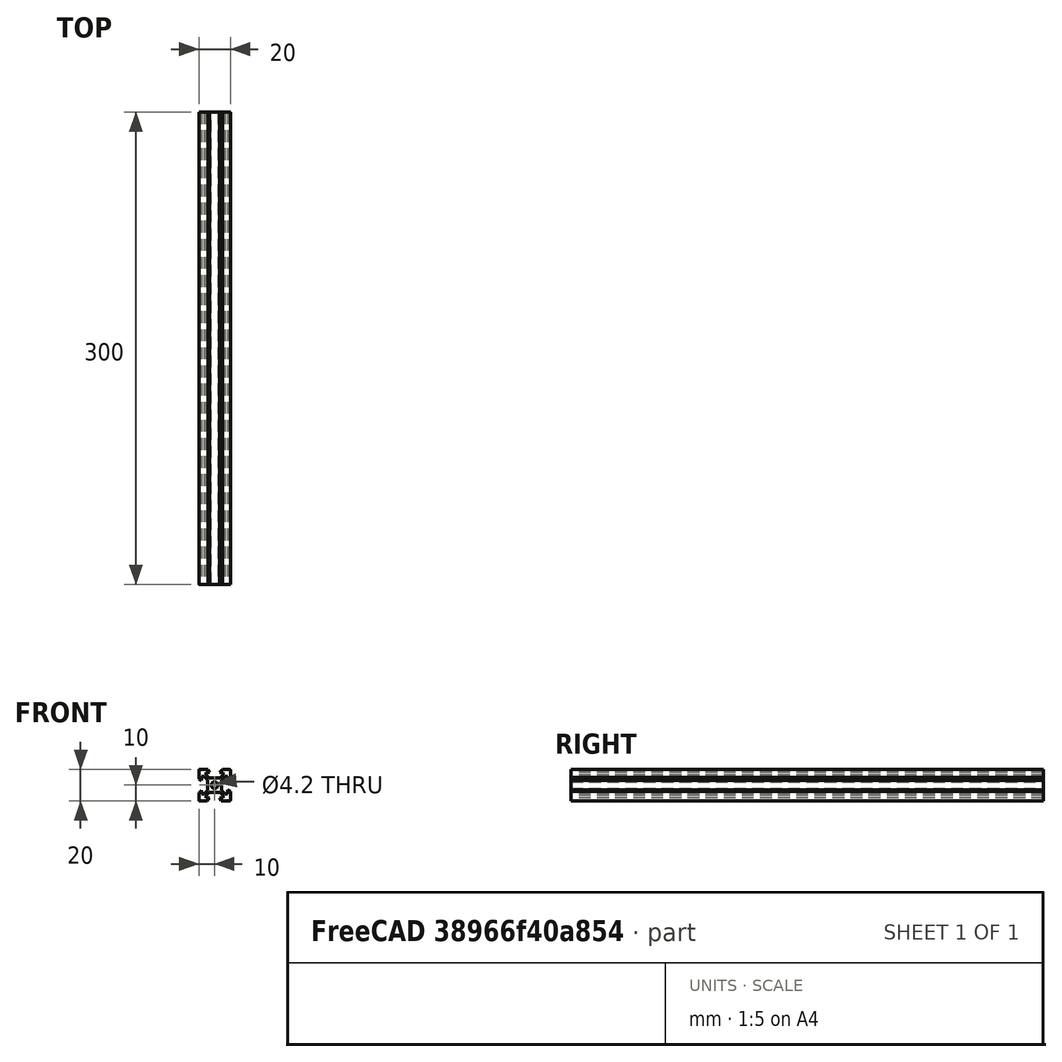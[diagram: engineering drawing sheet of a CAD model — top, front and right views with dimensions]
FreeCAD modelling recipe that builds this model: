
FCSTD DOCUMENT  (FreeCAD 0.20R29177 (Git))
Label: Slotted extrusion
License: All rights reserved
objects: Sketcher::SketchObject×1, PartDesign::Pad×1, PartDesign::Body×1
note: 4 computed .brp shape members not serialized (recipe doc carries the construction recipe); baked Part::Feature solids carry a one-line shape summary decoded from their .brp

FEATURE [Sketcher::SketchObject] Sketch
  FullyConstrained = true
  MapMode = 5
  Placement = pos=(0,0,0) rot=(1,0,0;1.5708rad)
  Support = -> [XZ_Plane]
  sketch-geometry (109):
    g0: LineSegment StartX=-10 StartY=10 StartZ=0 EndX=10 EndY=10 EndZ=0
    g1: LineSegment StartX=10 StartY=10 StartZ=0 EndX=10 EndY=-10 EndZ=0
    g2: LineSegment StartX=10 StartY=-10 StartZ=0 EndX=-10 EndY=-10 EndZ=0
    g3: LineSegment StartX=-10 StartY=-10 StartZ=0 EndX=-10 EndY=10 EndZ=0
    g4: LineSegment StartX=-8.2 StartY=8.2 StartZ=0 EndX=8.2 EndY=8.2 EndZ=0
    g5: LineSegment StartX=8.2 StartY=8.2 StartZ=0 EndX=8.2 EndY=-8.2 EndZ=0
    g6: LineSegment StartX=8.2 StartY=-8.2 StartZ=0 EndX=-8.2 EndY=-8.2 EndZ=0
    g7: LineSegment StartX=-8.2 StartY=-8.2 StartZ=0 EndX=-8.2 EndY=8.2 EndZ=0
    g8: LineSegment StartX=-4.5 StartY=4.5 StartZ=0 EndX=4.5 EndY=4.5 EndZ=0
    g9: LineSegment StartX=4.5 StartY=4.5 StartZ=0 EndX=4.5 EndY=-4.5 EndZ=0
    g10: LineSegment StartX=4.5 StartY=-4.5 StartZ=0 EndX=-4.5 EndY=-4.5 EndZ=0
    g11: LineSegment StartX=-4.5 StartY=-4.5 StartZ=0 EndX=-4.5 EndY=4.5 EndZ=0
    g12: LineSegment StartX=-8.2 StartY=5.5 StartZ=0 EndX=-8.2 EndY=3.1 EndZ=0
    g13: LineSegment StartX=-10 StartY=4.1 StartZ=0 EndX=-10 EndY=9.5 EndZ=0
    g14: LineSegment StartX=-9.5 StartY=10 StartZ=0 EndX=-4.1 EndY=10 EndZ=0
    g15: LineSegment StartX=-4.1 StartY=10 StartZ=0 EndX=-3.1 EndY=8.2 EndZ=0
    g16: LineSegment StartX=-3.1 StartY=8.2 StartZ=0 EndX=-5.5 EndY=8.2 EndZ=0
    g17: LineSegment StartX=3.1 StartY=8.2 StartZ=0 EndX=4.9 EndY=10 EndZ=0
    g18: LineSegment StartX=4.9 StartY=10 StartZ=0 EndX=9.5 EndY=10 EndZ=0
    g19: LineSegment StartX=10 StartY=9.5 StartZ=0 EndX=10 EndY=4.9 EndZ=0
    g20: LineSegment StartX=10 StartY=4.9 StartZ=0 EndX=8.2 EndY=3.1 EndZ=0
    g21: LineSegment StartX=-8.2 StartY=8.2 StartZ=0 EndX=-5.5 EndY=8.2 EndZ=0
    g22: LineSegment StartX=-5.5 StartY=8.2 StartZ=0 EndX=-5.5 EndY=5.5 EndZ=0
    g23: LineSegment StartX=-5.5 StartY=5.5 StartZ=0 EndX=-8.2 EndY=5.5 EndZ=0
    g24: LineSegment StartX=-8.2 StartY=5.5 StartZ=0 EndX=-8.2 EndY=8.2 EndZ=0
    g25: LineSegment StartX=5.5 StartY=8.2 StartZ=0 EndX=8.2 EndY=8.2 EndZ=0
    g26: LineSegment StartX=8.2 StartY=8.2 StartZ=0 EndX=8.2 EndY=5.5 EndZ=0
    g27: LineSegment StartX=8.2 StartY=5.5 StartZ=0 EndX=5.5 EndY=5.5 EndZ=0
    g28: LineSegment StartX=5.5 StartY=5.5 StartZ=0 EndX=5.5 EndY=8.2 EndZ=0
    g29: LineSegment StartX=3.1 StartY=8.2 StartZ=0 EndX=5.5 EndY=8.2 EndZ=0
    g30: LineSegment StartX=8.2 StartY=3.1 StartZ=0 EndX=8.2 EndY=5.5 EndZ=0
    g31: LineSegment StartX=-4.5 StartY=4.5 StartZ=0 EndX=-3.43934 EndY=4.5 EndZ=0
    g32: LineSegment StartX=-3.43934 StartY=4.5 StartZ=0 EndX=-3.43934 EndY=3.43934 EndZ=0
    g33: LineSegment StartX=-3.43934 StartY=3.43934 StartZ=0 EndX=-4.5 EndY=3.43934 EndZ=0
    g34: LineSegment StartX=-4.5 StartY=3.43934 StartZ=0 EndX=-4.5 EndY=4.5 EndZ=0
    g35: LineSegment StartX=-6.56066 StartY=6.56066 StartZ=0 EndX=-5.5 EndY=6.56066 EndZ=0
    g36: LineSegment StartX=-5.5 StartY=6.56066 StartZ=0 EndX=-5.5 EndY=5.5 EndZ=0
    g37: LineSegment StartX=-5.5 StartY=5.5 StartZ=0 EndX=-6.56066 EndY=5.5 EndZ=0
    g38: LineSegment StartX=-6.56066 StartY=5.5 StartZ=0 EndX=-6.56066 EndY=6.56066 EndZ=0
    g39: LineSegment StartX=-8.2 StartY=5.5 StartZ=0 EndX=-6.56066 EndY=5.5 EndZ=0
    g40: LineSegment StartX=-6.56066 StartY=5.5 StartZ=0 EndX=-4.5 EndY=3.43934 EndZ=0
    g41: LineSegment StartX=-5.5 StartY=8.2 StartZ=0 EndX=-5.5 EndY=6.56066 EndZ=0
    g42: LineSegment StartX=-3.43934 StartY=4.5 StartZ=0 EndX=-5.5 EndY=6.56066 EndZ=0
    g43: LineSegment StartX=3.43934 StartY=4.5 StartZ=0 EndX=4.5 EndY=4.5 EndZ=0
    g44: LineSegment StartX=4.5 StartY=4.5 StartZ=0 EndX=4.5 EndY=3.43934 EndZ=0
    g45: LineSegment StartX=4.5 StartY=3.43934 StartZ=0 EndX=3.43934 EndY=3.43934 EndZ=0
    g46: LineSegment StartX=3.43934 StartY=3.43934 StartZ=0 EndX=3.43934 EndY=4.5 EndZ=0
    g47: LineSegment StartX=5.5 StartY=6.56066 StartZ=0 EndX=6.56066 EndY=6.56066 EndZ=0
    g48: LineSegment StartX=6.56066 StartY=6.56066 StartZ=0 EndX=6.56066 EndY=5.5 EndZ=0
    g49: LineSegment StartX=6.56066 StartY=5.5 StartZ=0 EndX=5.5 EndY=5.5 EndZ=0
    g50: LineSegment StartX=5.5 StartY=5.5 StartZ=0 EndX=5.5 EndY=6.56066 EndZ=0
    g51: LineSegment StartX=8.2 StartY=5.5 StartZ=0 EndX=6.56066 EndY=5.5 EndZ=0
    g52: LineSegment StartX=6.56066 StartY=5.5 StartZ=0 EndX=4.5 EndY=3.43934 EndZ=0
    g53: LineSegment StartX=5.5 StartY=8.2 StartZ=0 EndX=5.5 EndY=6.56066 EndZ=0
    g54: LineSegment StartX=5.5 StartY=6.56066 StartZ=0 EndX=3.43934 EndY=4.5 EndZ=0
    g55: LineSegment StartX=3.43934 StartY=4.5 StartZ=0 EndX=-3.43934 EndY=4.5 EndZ=0
    g56: LineSegment StartX=4.5 StartY=3.43934 StartZ=0 EndX=4.5 EndY=-3.43934 EndZ=0
    g57: LineSegment StartX=8.2 StartY=-8.2 StartZ=0 EndX=5.5 EndY=-8.2 EndZ=0
    g58: LineSegment StartX=5.5 StartY=-8.2 StartZ=0 EndX=5.5 EndY=-5.5 EndZ=0
    g59: LineSegment StartX=5.5 StartY=-5.5 StartZ=0 EndX=8.2 EndY=-5.5 EndZ=0
    g60: LineSegment StartX=8.2 StartY=-5.5 StartZ=0 EndX=8.2 EndY=-8.2 EndZ=0
    g61: LineSegment StartX=3.43934 StartY=-3.43934 StartZ=0 EndX=4.5 EndY=-3.43934 EndZ=0
    g62: LineSegment StartX=4.5 StartY=-3.43934 StartZ=0 EndX=4.5 EndY=-4.5 EndZ=0
    g63: LineSegment StartX=4.5 StartY=-4.5 StartZ=0 EndX=3.43934 EndY=-4.5 EndZ=0
    g64: LineSegment StartX=3.43934 StartY=-4.5 StartZ=0 EndX=3.43934 EndY=-3.43934 EndZ=0
    g65: LineSegment StartX=5.5 StartY=-5.5 StartZ=0 EndX=6.56066 EndY=-5.5 EndZ=0
    g66: LineSegment StartX=6.56066 StartY=-5.5 StartZ=0 EndX=6.56066 EndY=-6.56066 EndZ=0
    g67: LineSegment StartX=6.56066 StartY=-6.56066 StartZ=0 EndX=5.5 EndY=-6.56066 EndZ=0
    g68: LineSegment StartX=5.5 StartY=-6.56066 StartZ=0 EndX=5.5 EndY=-5.5 EndZ=0
    g69: LineSegment StartX=4.5 StartY=-3.43934 StartZ=0 EndX=6.56066 EndY=-5.5 EndZ=0
    g70: LineSegment StartX=5.5 StartY=-6.56066 StartZ=0 EndX=3.43934 EndY=-4.5 EndZ=0
    g71: LineSegment StartX=6.56066 StartY=-5.5 StartZ=0 EndX=8.2 EndY=-5.5 EndZ=0
    g72: LineSegment StartX=8.2 StartY=-5.5 StartZ=0 EndX=8.2 EndY=-3.1 EndZ=0
    g73: LineSegment StartX=8.2 StartY=-3.1 StartZ=0 EndX=10 EndY=-4.1 EndZ=0
    g74: LineSegment StartX=10 StartY=-4.1 StartZ=0 EndX=10 EndY=-9.5 EndZ=0
    g75: LineSegment StartX=3.1 StartY=-8.2 StartZ=0 EndX=5.5 EndY=-8.2 EndZ=0
    g76: LineSegment StartX=5.5 StartY=-8.2 StartZ=0 EndX=5.5 EndY=-6.56066 EndZ=0
    g77: LineSegment StartX=4.1 StartY=-10 StartZ=0 EndX=9.5 EndY=-10 EndZ=0
    g78: LineSegment StartX=4.1 StartY=-10 StartZ=0 EndX=3.1 EndY=-8.2 EndZ=0
    g79: LineSegment StartX=-10 StartY=4.1 StartZ=0 EndX=-8.2 EndY=3.1 EndZ=0
    g80: LineSegment StartX=-4.5 StartY=-3.43934 StartZ=0 EndX=-3.43934 EndY=-3.43934 EndZ=0
    g81: LineSegment StartX=-3.43934 StartY=-3.43934 StartZ=0 EndX=-3.43934 EndY=-4.5 EndZ=0
    g82: LineSegment StartX=-3.43934 StartY=-4.5 StartZ=0 EndX=-4.5 EndY=-4.5 EndZ=0
    g83: LineSegment StartX=-4.5 StartY=-4.5 StartZ=0 EndX=-4.5 EndY=-3.43934 EndZ=0
    g84: LineSegment StartX=-8.2 StartY=-5.5 StartZ=0 EndX=-5.5 EndY=-5.5 EndZ=0
    g85: LineSegment StartX=-5.5 StartY=-5.5 StartZ=0 EndX=-5.5 EndY=-8.2 EndZ=0
    g86: LineSegment StartX=-5.5 StartY=-8.2 StartZ=0 EndX=-8.2 EndY=-8.2 EndZ=0
    g87: LineSegment StartX=-8.2 StartY=-8.2 StartZ=0 EndX=-8.2 EndY=-5.5 EndZ=0
    g88: LineSegment StartX=-6.56066 StartY=-5.5 StartZ=0 EndX=-5.5 EndY=-5.5 EndZ=0
    g89: LineSegment StartX=-5.5 StartY=-5.5 StartZ=0 EndX=-5.5 EndY=-6.56066 EndZ=0
    g90: LineSegment StartX=-5.5 StartY=-6.56066 StartZ=0 EndX=-6.56066 EndY=-6.56066 EndZ=0
    g91: LineSegment StartX=-6.56066 StartY=-6.56066 StartZ=0 EndX=-6.56066 EndY=-5.5 EndZ=0
    g92: LineSegment StartX=-5.5 StartY=-6.56066 StartZ=0 EndX=-3.43934 EndY=-4.5 EndZ=0
    g93: LineSegment StartX=-3.43934 StartY=-4.5 StartZ=0 EndX=3.43934 EndY=-4.5 EndZ=0
    g94: LineSegment StartX=-5.5 StartY=-6.56066 StartZ=0 EndX=-5.5 EndY=-8.2 EndZ=0
    g95: LineSegment StartX=-5.5 StartY=-8.2 StartZ=0 EndX=-3.2 EndY=-8.2 EndZ=0
    g96: LineSegment StartX=-3.2 StartY=-8.2 StartZ=0 EndX=-4.9 EndY=-10 EndZ=0
    g97: LineSegment StartX=-4.9 StartY=-10 StartZ=0 EndX=-9.5 EndY=-10 EndZ=0
    g98: LineSegment StartX=-10 StartY=-9.5 StartZ=0 EndX=-10 EndY=-4.9 EndZ=0
    g99: LineSegment StartX=-10 StartY=-4.9 StartZ=0 EndX=-8.2 EndY=-3.2 EndZ=0
    g100: LineSegment StartX=-8.2 StartY=-3.2 StartZ=0 EndX=-8.2 EndY=-5.5 EndZ=0
    g101: LineSegment StartX=-8.2 StartY=-5.5 StartZ=0 EndX=-6.56066 EndY=-5.5 EndZ=0
    g102: LineSegment StartX=-6.56066 StartY=-5.5 StartZ=0 EndX=-4.5 EndY=-3.43934 EndZ=0
    g103: LineSegment StartX=-4.5 StartY=-3.43934 StartZ=0 EndX=-4.5 EndY=3.43934 EndZ=0
    g104: Circle CenterX=0 CenterY=0 CenterZ=0 NormalX=0 NormalY=0 NormalZ=1 AngleXU=0 Radius=2.1
    g105: ArcOfCircle CenterX=-9.5 CenterY=9.5 CenterZ=0 NormalX=0 NormalY=0 NormalZ=1 AngleXU=0 Radius=0.5 StartAngle=1.5708 EndAngle=3.14159
    g106: ArcOfCircle CenterX=9.5 CenterY=9.5 CenterZ=0 NormalX=0 NormalY=0 NormalZ=1 AngleXU=0 Radius=0.5 StartAngle=6e-16 EndAngle=1.5708
    g107: ArcOfCircle CenterX=9.5 CenterY=-9.5 CenterZ=0 NormalX=0 NormalY=0 NormalZ=1 AngleXU=0 Radius=0.5 StartAngle=4.71239 EndAngle=6.28319
    g108: ArcOfCircle CenterX=-9.5 CenterY=-9.5 CenterZ=0 NormalX=0 NormalY=0 NormalZ=1 AngleXU=0 Radius=0.5 StartAngle=3.14159 EndAngle=4.71239
  constraints (286):
    c: Coincident(g0,g1)
    c: Coincident(g1,g2)
    c: Coincident(g2,g3)
    c: Coincident(g3,g0)
    c: Horizontal(g0)
    c: Horizontal(g2)
    c: Vertical(g1)
    c: Vertical(g3)
    c: Equal(g0,g3)
    c: DistanceY(g3,g3) = 20
    c: Symmetric(g0,g2,g-1)
    c: Coincident(g4,g5)
    c: Coincident(g5,g6)
    c: Coincident(g6,g7)
    c: Coincident(g7,g4)
    c: Horizontal(g4)
    c: Horizontal(g6)
    c: Vertical(g5)
    c: Vertical(g7)
    c: Equal(g4,g7)
    c: DistanceX(g0,g4) = 1.8
    c: DistanceX(g5,g1) = 1.8
    c: DistanceY(g4,g0) = 1.8
    c: Coincident(g8,g9)
    c: Coincident(g9,g10)
    c: Coincident(g10,g11)
    c: Coincident(g11,g8)
    c: Horizontal(g8)
    c: Horizontal(g10)
    c: Vertical(g9)
    c: Vertical(g11)
    c: Equal(g8,g11)
    c: Symmetric(g9,g8,g-1)
    c: PointOnObject(g12,g7)
    c: PointOnObject(g13,g3)
    c: Coincident(g14,g15)
    c: PointOnObject(g15,g4)
    c: Coincident(g15,g16)
    c: PointOnObject(g14,g0)
    c: PointOnObject(g12,g7)
    c: PointOnObject(g16,g4)
    c: Equal(g12,g16)
    c: PointOnObject(g17,g0)
    c: Coincident(g17,g18)
    c: Vertical(g19)
    c: Coincident(g19,g20)
    c: PointOnObject(g20,g5)
    c: Parallel(g17,g20)
    c: Equal(g18,g19)
    c: DistanceX(g15,g17) = 6.2
    c: DistanceX(g14,g17) = 9
    c: Coincident(g21,g22)
    c: Coincident(g22,g23)
    c: Coincident(g23,g24)
    c: Coincident(g24,g21)
    c: Horizontal(g21)
    c: Horizontal(g23)
    c: Vertical(g22)
    c: Vertical(g24)
    c: Coincident(g21,g4)
    c: Equal(g22,g23)
    c: PointOnObject(g17,g4)
    c: Coincident(g25,g26)
    c: Coincident(g26,g27)
    c: Coincident(g27,g28)
    c: Coincident(g28,g25)
    c: Horizontal(g25)
    c: Horizontal(g27)
    c: Vertical(g26)
    c: Vertical(g28)
    c: Equal(g25,g28)
    c: Coincident(g25,g4)
    c: Coincident(g29,g17)
    c: Equal(g16,g29)
    c: Coincident(g29,g25)
    c: DistanceX(g22,g27) = 11
    c: Equal(g27,g23)
    c: Coincident(g30,g20)
    c: Coincident(g30,g26)
    c: Equal(g29,g30)
    c: Coincident(g31,g32)
    c: Coincident(g32,g33)
    c: Coincident(g33,g34)
    c: Coincident(g34,g31)
    c: Horizontal(g31)
    c: Horizontal(g33)
    c: Vertical(g32)
    c: Vertical(g34)
    c: Equal(g31,g34)
    c: Coincident(g31,g8)
    c: Distance(g33,g31) = 1.5
    c: Coincident(g35,g36)
    c: Coincident(g36,g37)
    c: Coincident(g37,g38)
    c: Coincident(g38,g35)
    c: Horizontal(g35)
    c: Horizontal(g37)
    c: Vertical(g36)
    c: Vertical(g38)
    c: Equal(g35,g38)
    c: Distance(g35,g37) = 1.5
    c: Coincident(g36,g22)
    c: Coincident(g39,g12)
    c: Coincident(g39,g37)
    c: Horizontal(g39)
    c: Coincident(g40,g39)
    c: Coincident(g40,g33)
    c: Coincident(g41,g16)
    c: Coincident(g41,g35)
    c: Vertical(g41)
    c: Coincident(g42,g31)
    c: Coincident(g42,g41)
    c: Coincident(g43,g44)
    c: Coincident(g44,g45)
    c: Coincident(g45,g46)
    c: Coincident(g46,g43)
    c: Horizontal(g43)
    c: Horizontal(g45)
    c: Vertical(g44)
    c: Vertical(g46)
    c: Coincident(g47,g48)
    c: Coincident(g48,g49)
    c: Coincident(g49,g50)
    c: Coincident(g50,g47)
    c: Horizontal(g47)
    c: Horizontal(g49)
    c: Vertical(g48)
    c: Vertical(g50)
    c: Equal(g43,g46)
    c: Coincident(g43,g8)
    c: Equal(g47,g50)
    c: Distance(g48,g47) = 1.5
    c: Coincident(g49,g27)
    c: Coincident(g51,g30)
    c: Coincident(g52,g51)
    c: Coincident(g52,g44)
    c: Coincident(g29,g53)
    c: Coincident(g53,g54)
    c: Coincident(g54,g43)
    c: Coincident(g54,g55)
    c: Coincident(g55,g42)
    c: Coincident(g53,g47)
    c: Coincident(g51,g48)
    c: Coincident(g52,g56)
    c: Distance(g54,g52) = 1.5
    c: Coincident(g57,g58)
    c: Coincident(g58,g59)
    c: Coincident(g59,g60)
    c: Coincident(g60,g57)
    c: Horizontal(g57)
    c: Horizontal(g59)
    c: Vertical(g58)
    c: Vertical(g60)
    c: Coincident(g61,g62)
    c: Coincident(g62,g63)
    c: Coincident(g63,g64)
    c: Coincident(g64,g61)
    c: Horizontal(g61)
    c: Horizontal(g63)
    c: Vertical(g62)
    c: Vertical(g64)
    c: Equal(g59,g58)
    c: Distance(g61,g63) = 1.5
    c: Coincident(g62,g9)
    c: Equal(g61,g64)
    c: Coincident(g57,g5)
    c: Coincident(g65,g66)
    c: Coincident(g66,g67)
    c: Coincident(g67,g68)
    c: Coincident(g68,g65)
    c: Horizontal(g65)
    c: Horizontal(g67)
    c: Vertical(g66)
    c: Vertical(g68)
    c: Equal(g65,g68)
    c: Distance(g65,g67) = 1.5
    c: Coincident(g65,g58)
    c: Coincident(g69,g56)
    c: Coincident(g69,g65)
    c: Coincident(g70,g67)
    c: Coincident(g70,g63)
    c: Coincident(g56,g61)
    c: Coincident(g69,g71)
    c: Coincident(g71,g72)
    c: Vertical(g72)
    c: Coincident(g72,g73)
    c: PointOnObject(g73,g1)
    c: Coincident(g73,g74)
    c: PointOnObject(g75,g6)
    c: Coincident(g75,g76)
    c: Coincident(g76,g70)
    c: Coincident(g71,g59)
    c: Coincident(g75,g57)
    c: PointOnObject(g77,g2)
    c: Equal(g72,g75)
    c: DistanceY(g72,g20) = 6.2
    c: DistanceY(g73,g19) = 9
    c: DistanceY(g69,g51) = 11
    c: Equal(g74,g77)
    c: Coincident(g78,g77)
    c: Coincident(g78,g75)
    c: Equal(g14,g13)
    c: Coincident(g79,g13)
    c: Coincident(g79,g12)
    c: Coincident(g80,g81)
    c: Coincident(g81,g82)
    c: Coincident(g82,g83)
    c: Coincident(g83,g80)
    c: Horizontal(g80)
    c: Horizontal(g82)
    c: Vertical(g81)
    c: Vertical(g83)
    c: Coincident(g84,g85)
    c: Coincident(g85,g86)
    c: Coincident(g86,g87)
    c: Coincident(g87,g84)
    c: Horizontal(g84)
    c: Horizontal(g86)
    c: Vertical(g85)
    c: Vertical(g87)
    c: Coincident(g88,g89)
    c: Coincident(g89,g90)
    c: Coincident(g90,g91)
    c: Coincident(g91,g88)
    c: Horizontal(g88)
    c: Horizontal(g90)
    c: Vertical(g89)
    c: Vertical(g91)
    c: Equal(g85,g84)
    c: Coincident(g86,g6)
    c: Equal(g89,g88)
    c: Distance(g89,g88) = 1.5
    c: Coincident(g84,g88)
    c: Equal(g82,g83)
    c: Distance(g81,g80) = 1.5
    c: Coincident(g82,g10)
    c: Coincident(g92,g89)
    c: Coincident(g92,g81)
    c: Coincident(g93,g92)
    c: Coincident(g93,g70)
    c: Coincident(g92,g94)
    c: Coincident(g94,g95)
    c: Coincident(g95,g96)
    c: Coincident(g96,g97)
    c: Horizontal(g97)
    c: Coincident(g98,g99)
    c: Coincident(g99,g100)
    c: Coincident(g100,g101)
    c: Coincident(g101,g88)
    c: Coincident(g101,g102)
    c: Coincident(g102,g80)
    c: Coincident(g100,g84)
    c: PointOnObject(g99,g7)
    c: PointOnObject(g98,g3)
    c: Coincident(g94,g85)
    c: PointOnObject(g95,g6)
    c: Equal(g97,g98)
    c: Equal(g100,g95)
    c: Coincident(g103,g102)
    c: Coincident(g103,g40)
    c: DistanceX(g96,g77) = 9
    c: DistanceX(g95,g75) = 6.3
    c: DistanceX(g84,g70) = 11
    c: DistanceX(g22,g8) = 1
    c: Coincident(g104,g-1)
    c: Radius(g104) = 2.1
    c: Tangent(g14,g105) = 1.5708
    c: Tangent(g13,g105) = 1.5708
    c: PointOnObject(g14,g0)
    c: PointOnObject(g13,g3)
    c: Radius(g105) = 0.5
    c: Tangent(g18,g106) = 1.5708
    c: Tangent(g19,g106) = 1.5708
    c: PointOnObject(g19,g1)
    c: PointOnObject(g18,g0)
    c: Radius(g106) = 0.5
    c: Tangent(g74,g107) = 1.5708
    c: Tangent(g77,g107) = -1.5708
    c: PointOnObject(g74,g1)
    c: PointOnObject(g77,g2)
    c: Radius(g107) = 0.5
    c: Tangent(g97,g108) = 1.5708
    c: Tangent(g98,g108) = 1.5708
    c: PointOnObject(g98,g3)
    c: PointOnObject(g97,g2)
    c: Radius(g108) = 0.5
FEATURE [PartDesign::Pad] Pad
  Direction = (0,-1,2e-16)
  Length = 300
  Length2 = 10
  Placement = pos=(0,0,0) rot=(1,0,0;1.5708rad)
  Profile = -> Sketch
  ReferenceAxis = -> Sketch [N_Axis]
  Type = 0
FEATURE [PartDesign::Body] Body
  Group = -> [Sketch,Pad]
  Origin = -> Origin
  Tip = -> Pad
